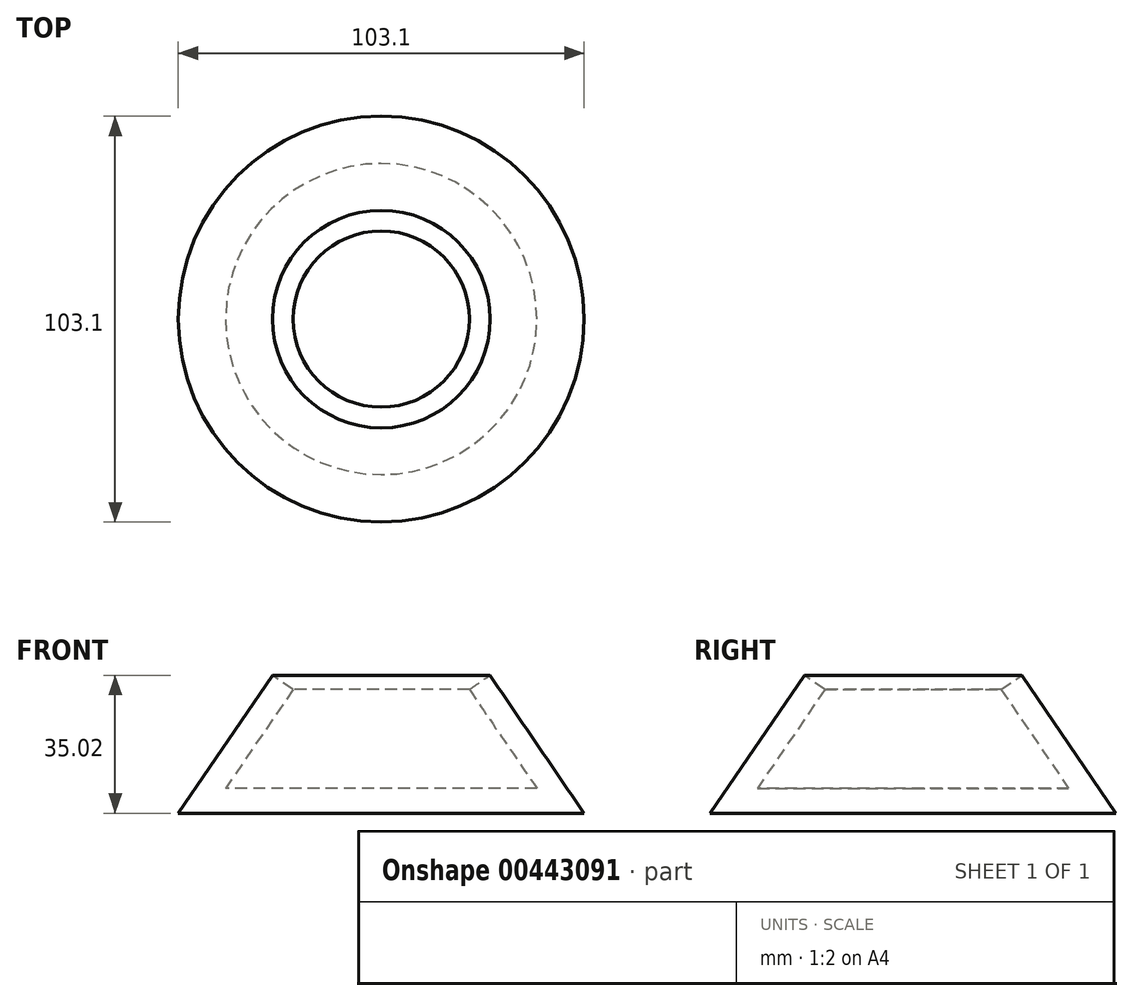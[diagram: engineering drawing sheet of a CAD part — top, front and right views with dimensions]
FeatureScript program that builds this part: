
annotation { "Feature Type Name" : "Feature", "Feature Type Description" : "" }
export const myFeature = defineFeature(function(context is Context, id is Id, definition is map)
    precondition{}
    {
        {
            var Q0;
            Q0=qCreatedBy(makeId("Front.planeOp"),FACE);
            var sketch = newSketch(context, id + "F0", { "sketchPlane" : qUnion([Q0])});
            skLineSegment(sketch, "E0", {"start": v(0, 24.5) * mm, "end": v(-51.55, 24.5) * mm});
            skLineSegment(sketch, "E1", {"start": v(-51.55, 24.5) * mm, "end": v(-27.64, 59.52) * mm});
            skLineSegment(sketch, "E2.0", {"start": v(-39.52, 30.85) * mm, "end": v(-22.4, 55.94) * mm});
            skLineSegment(sketch, "E2.1", {"start": v(0, 30.85) * mm, "end": v(-39.52, 30.85) * mm});
            skLineSegment(sketch, "E3", {"start": v(0, 30.85) * mm, "end": v(0, 24.5) * mm});
            skLineSegment(sketch, "E4", {"start": v(-27.64, 59.52) * mm, "end": v(-22.4, 55.94) * mm});
            skSolve(sketch);
        }
        {
            var Q0;
            Q0=makeQuery(id+"F0.imprint","IMPRINT",FACE,{"disambiguationData":[TD([[makeQuery(id+"F0.imprint","IMPRINT",EDGE,{"derivedFrom":sQuery(id+"F0.wireOp",EDGE,"E0")}),-1.0]])]});
            var Q1;
            Q1=sQuery(id+"F0.wireOp",EDGE,"E3");
            revolve(context, id + "F1", {"entities" : qUnion([Q0]), "axis" : qUnion([Q1]), "revolveType" : RevolveType.FULL});
        }
    });
